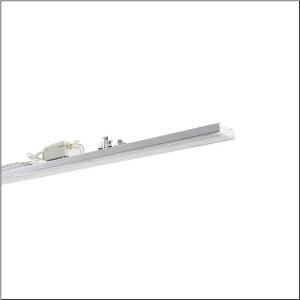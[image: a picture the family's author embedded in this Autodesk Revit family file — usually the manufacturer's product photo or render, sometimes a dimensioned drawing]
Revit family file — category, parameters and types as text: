
# Revit family: licross_r__21_recessed_ho_52tl12dn4fxmd_dc4c
name_source: partatom
category: Lighting Fixtures
units: mm (PartAtom-declared; Revit-internal decimal feet)

## family parameters
Cut with Voids When Loaded = No
Host = Face
Light Source = No
Part Type = Normal
Room Calculation Point = No
Round Connector Dimension = Use Diameter
Shared = No

## types (1)
- --- (1 x LED, 2250 lm, 14 W, 4000K)
    Apparent Load = 14 VA
    CIE Flux Codes = 69 91 98 100 100
    Color Rendering = 80
    Color Temperature = 4000K
    Default Elevation = 1800 mm
    Description = Licross® 21 Recessed HO, luminaire insert, of sheet steel, galvanised, coil coated, white, length: 1.500mm, width: 66mm, height: 67mm, LED rated luminous flux: 15.000lm, light colour: 840, control gear: DALI 2, with plug, 6-pole, with phase selection, mains connection: 220..240V, AC/DC, 0/50..60Hz, rated input power: 85W, without changeover relay, for emergency light function, for central battery installations according to DIN EN 60598-2-22, halogen-free wiring, primary optical cover: cover, of PMMA, light emission: direct distribution, primary light characteristic: symmetric, protection rating (complete): IP40, insulation class (complete): insulation class I (protective earthing), certification: CE, ENEC, VDE, UKCA, protection symbol: D if used in an environment without relevant dust loads with corresponding accessories, impact resistance: IK06, permissible ambient temperature for indoor applications: -25..+30°C, standard: EN 60598-2-22, corresponds to IFS (International Featured Standards) requirements for safety and quality in the food industry, reducing of maximum allowable ambient temperature of 5°C with ceiling mounting, LABS conformity tested according to VDMA 24364:2018-05, packaging unit: 1 piece
    Height = 58 mm
    Lamp = 1 x LED
    Lamp Light Flux = 2250 lm
    Lamp Power = 14 W
    Lamp count = 1
    Length = 1500 mm
    Luminous efficacy = 161 lm/W
    Manufacturer = Siteco
    ModVariant = No
    Model = 52TL12DN4FXMD
    Mounting Place = Ceiling
    Mounting Type = Pendant
    Number of Poles = 1
    OnlyDefault = Yes
    Power Factor = 1
    Product Name = Licross® 21 Recessed HO
    Product group = luminaire insert
    ProductGroupID = 901
    Protection Class = Protection class I
    Protection Degree = IP 40
    RLX_Detail_Level = 1
    RLX_Emergency_Light_Flux = 0 lm
    RLX_Emergency_Type = 0
    RLX_Emergency_Type_DB = No
    RlxData = <blob elided: 25133 chars, md5=b11ed785>
    Socket = socket
    Standby Power = 0 W
    System Light Flux = 2250 lm
    System Power = 14 W
    Type Comments = : DC mode (central or group accumulator) initial emergency light level
    Type Image = l_1296930.jpg
    URL = http://relux.com
    VarID = @adj_041853
    Voltage = 0 V
    Weight = 0.00 kg
    Width = 66 mm

## geometry (parser evidence)
native form markers: Blend x4, Sweep x12
no freeform markers — native parametric forms only
